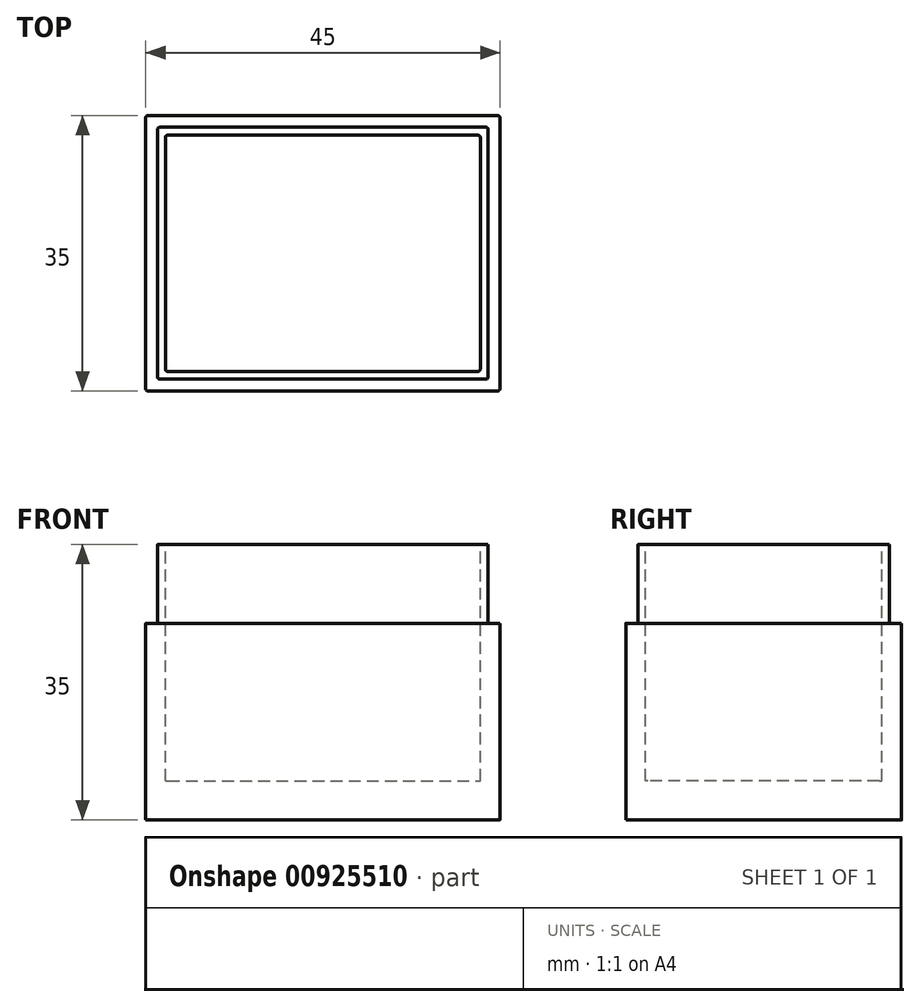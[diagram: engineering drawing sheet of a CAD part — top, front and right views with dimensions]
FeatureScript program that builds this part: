
annotation { "Feature Type Name" : "Feature", "Feature Type Description" : "" }
export const myFeature = defineFeature(function(context is Context, id is Id, definition is map)
    precondition{}
    {
        {
            var Q0;
            Q0=qCreatedBy(makeId("Top.planeOp"),FACE);
            var sketch = newSketch(context, id + "F0", { "sketchPlane" : qUnion([Q0])});
            skLineSegment(sketch, "E0.bottom", {"start": v(-22.5, 17.5) * mm, "end": v(22.5, 17.5) * mm});
            skLineSegment(sketch, "E0.top", {"start": v(-22.5, -17.5) * mm, "end": v(22.5, -17.5) * mm});
            skLineSegment(sketch, "E0.left", {"start": v(-22.5, 17.5) * mm, "end": v(-22.5, -17.5) * mm});
            skLineSegment(sketch, "E0.right", {"start": v(22.5, 17.5) * mm, "end": v(22.5, -17.5) * mm});
            skPoint(sketch, "E0.middle", {"position": v(0, 0) * mm});
            skSolve(sketch);
        }
        {
            var Q0;
            Q0=makeQuery(id+"F0.imprint","IMPRINT",FACE,{"disambiguationData":[TD([[makeQuery(id+"F0.imprint","IMPRINT",EDGE,{"derivedFrom":sQuery(id+"F0.wireOp",EDGE,"E0.bottom")}),-1.0]])]});
            extrude(context, id + "F1", {"entities" : qUnion([Q0]), "depth" : 35 * mm, "offsetDistance" : 25 * mm});
        }
        {
            var Q0;
            Q0=makeQuery(id+"F1.opExtrude","CAP_FACE",FACE,{"disambiguationData":[OSD([sQuery(id+"F0.wireOp",EDGE,"E0.bottom"),sQuery(id+"F0.wireOp",EDGE,"E0.top"),sQuery(id+"F0.wireOp",EDGE,"E0.left"),sQuery(id+"F0.wireOp",EDGE,"E0.right")])],"isStart":false});
            var sketch = newSketch(context, id + "F2", { "sketchPlane" : qUnion([Q0])});
            skLineSegment(sketch, "E1.bottom", {"start": v(-20, 15) * mm, "end": v(20, 15) * mm});
            skLineSegment(sketch, "E1.top", {"start": v(-20, -15) * mm, "end": v(20, -15) * mm});
            skLineSegment(sketch, "E1.left", {"start": v(-20, 15) * mm, "end": v(-20, -15) * mm});
            skLineSegment(sketch, "E1.right", {"start": v(20, 15) * mm, "end": v(20, -15) * mm});
            skPoint(sketch, "E1.middle", {"position": v(0, 0) * mm});
            skSolve(sketch);
        }
        {
            var Q0;
            Q0=makeQuery(id+"F2.imprint","IMPRINT",FACE,{"disambiguationData":[TD([[makeQuery(id+"F2.imprint","IMPRINT",EDGE,{"derivedFrom":sQuery(id+"F2.wireOp",EDGE,"E1.bottom")}),-1.0]])]});
            extrude(context, id + "F3", {"entities" : qUnion([Q0]), "operationType" : NewBodyOperationType.REMOVE, "oppositeDirection" : true, "depth" : 30 * mm, "offsetDistance" : 25 * mm});
        }
        {
            var Q0;
            Q0=makeQuery(id+"F1.opExtrude","CAP_FACE",FACE,{"disambiguationData":[OSD([sQuery(id+"F0.wireOp",EDGE,"E0.bottom"),sQuery(id+"F0.wireOp",EDGE,"E0.top"),sQuery(id+"F0.wireOp",EDGE,"E0.left"),sQuery(id+"F0.wireOp",EDGE,"E0.right")])],"isStart":false});
            var sketch = newSketch(context, id + "F4", { "sketchPlane" : qUnion([Q0])});
            skLineSegment(sketch, "E2.bottom", {"start": v(-21, 16) * mm, "end": v(21, 16) * mm});
            skLineSegment(sketch, "E2.top", {"start": v(-21, -16) * mm, "end": v(21, -16) * mm});
            skLineSegment(sketch, "E2.left", {"start": v(-21, 16) * mm, "end": v(-21, -16) * mm});
            skLineSegment(sketch, "E2.right", {"start": v(21, 16) * mm, "end": v(21, -16) * mm});
            skPoint(sketch, "E2.middle", {"position": v(0, 0) * mm});
            skSolve(sketch);
        }
        {
            var Q0;
            Q0=makeQuery(id+"F4.imprint","IMPRINT",FACE,{"disambiguationData":[TD([[makeQuery(id+"F4.imprint","IMPRINT",EDGE,{"derivedFrom":sQuery(id+"F4.wireOp",EDGE,"E2.bottom")}),1.0]])]});
            extrude(context, id + "F5", {"entities" : qUnion([Q0]), "operationType" : NewBodyOperationType.REMOVE, "oppositeDirection" : true, "depth" : 10 * mm, "offsetDistance" : 25 * mm});
        }
        {
            var Q0;
            Q0=makeQuery(id+"F1.opExtrude","SWEPT_EDGE",EDGE,{"disambiguationData":[OSD([sQuery(id+"F0.wireOp",EDGE,"E0.bottom"),sQuery(id+"F0.wireOp",EDGE,"E0.left")])]});
            var Q1;
            Q1=makeQuery(id+"F1.opExtrude","SWEPT_EDGE",EDGE,{"disambiguationData":[OSD([sQuery(id+"F0.wireOp",EDGE,"E0.bottom"),sQuery(id+"F0.wireOp",EDGE,"E0.right")])]});
            var Q2;
            Q2=makeQuery(id+"F1.opExtrude","SWEPT_EDGE",EDGE,{"disambiguationData":[OSD([sQuery(id+"F0.wireOp",EDGE,"E0.top"),sQuery(id+"F0.wireOp",EDGE,"E0.right")])]});
            var Q3;
            Q3=makeQuery(id+"F1.opExtrude","SWEPT_EDGE",EDGE,{"disambiguationData":[OSD([sQuery(id+"F0.wireOp",EDGE,"E0.top"),sQuery(id+"F0.wireOp",EDGE,"E0.left")])]});
            var Q4;
            Q4=makeQuery(id+"F5.boolean.opBoolean","COPY",EDGE,{"derivedFrom":makeQuery(id+"F5.opExtrude","SWEPT_EDGE",EDGE,{"disambiguationData":[OSD([sQuery(id+"F4.wireOp",EDGE,"E2.top"),sQuery(id+"F4.wireOp",EDGE,"E2.left")])]})});
            var Q5;
            Q5=makeQuery(id+"F5.boolean.opBoolean","COPY",EDGE,{"derivedFrom":makeQuery(id+"F5.opExtrude","SWEPT_EDGE",EDGE,{"disambiguationData":[OSD([sQuery(id+"F4.wireOp",EDGE,"E2.top"),sQuery(id+"F4.wireOp",EDGE,"E2.right")])]})});
            var Q6;
            Q6=makeQuery(id+"F5.boolean.opBoolean","COPY",EDGE,{"derivedFrom":makeQuery(id+"F5.opExtrude","SWEPT_EDGE",EDGE,{"disambiguationData":[OSD([sQuery(id+"F4.wireOp",EDGE,"E2.bottom"),sQuery(id+"F4.wireOp",EDGE,"E2.right")])]})});
            var Q7;
            Q7=makeQuery(id+"F5.boolean.opBoolean","COPY",EDGE,{"derivedFrom":makeQuery(id+"F5.opExtrude","SWEPT_EDGE",EDGE,{"disambiguationData":[OSD([sQuery(id+"F4.wireOp",EDGE,"E2.bottom"),sQuery(id+"F4.wireOp",EDGE,"E2.left")])]})});
            var Q8;
            Q8=makeQuery(id+"F3.boolean.opBoolean","COPY",EDGE,{"derivedFrom":makeQuery(id+"F3.opExtrude","SWEPT_EDGE",EDGE,{"disambiguationData":[OSD([sQuery(id+"F2.wireOp",EDGE,"E1.bottom"),sQuery(id+"F2.wireOp",EDGE,"E1.left")])]})});
            var Q9;
            Q9=makeQuery(id+"F3.boolean.opBoolean","COPY",EDGE,{"derivedFrom":makeQuery(id+"F3.opExtrude","SWEPT_EDGE",EDGE,{"disambiguationData":[OSD([sQuery(id+"F2.wireOp",EDGE,"E1.bottom"),sQuery(id+"F2.wireOp",EDGE,"E1.right")])]})});
            var Q10;
            Q10=makeQuery(id+"F3.boolean.opBoolean","COPY",EDGE,{"derivedFrom":makeQuery(id+"F3.opExtrude","SWEPT_EDGE",EDGE,{"disambiguationData":[OSD([sQuery(id+"F2.wireOp",EDGE,"E1.top"),sQuery(id+"F2.wireOp",EDGE,"E1.right")])]})});
            var Q11;
            Q11=makeQuery(id+"F3.boolean.opBoolean","COPY",EDGE,{"derivedFrom":makeQuery(id+"F3.opExtrude","SWEPT_EDGE",EDGE,{"disambiguationData":[OSD([sQuery(id+"F2.wireOp",EDGE,"E1.top"),sQuery(id+"F2.wireOp",EDGE,"E1.left")])]})});
            fillet(context, id + "F6", {"entities" : qUnion([Q0, Q1, Q2, Q3, Q4, Q5, Q6, Q7, Q8, Q9, Q10, Q11]), "radius" : 0.3 * mm, "tangentPropagation" : true, "allowEdgeOverflow" : false});
        }
    });
